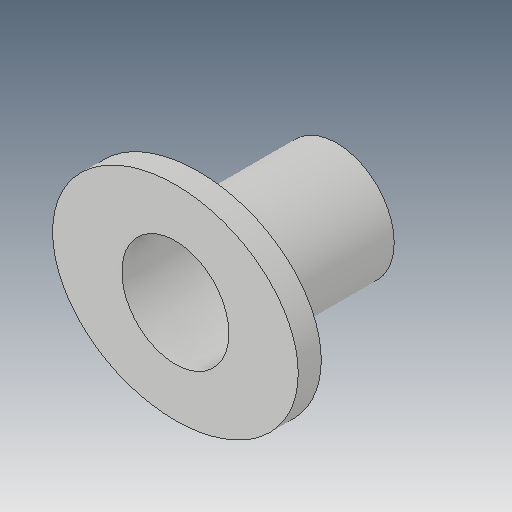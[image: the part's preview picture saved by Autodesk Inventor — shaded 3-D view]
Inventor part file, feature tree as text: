
AUTODESK INVENTOR PART (.ipt)
format: ipt  version: 2017 (Build 210142000, 142)  size: 117,760 bytes
history: native  units: mm
features: extrude x4, sketch x4, other x2, reference x1, projected_geometry x1
ambient origin geometry x8: Origin, YZ Plane, XZ Plane, XY Plane, X Axis, Y Axis, Z Axis, Center Point
bodies: Solid1 (feature_tree)
feature tree (12):
  extrude  "Extrusion1"  Depth=1.0mm TaperAngle=0.0deg
  extrude  "Extrusion2"  Depth=1.0mm TaperAngle=0.0deg
  extrude  "Extrusion3"  [1 undecoded]
  extrude  "Extrusion4"  [1 undecoded]
  sketch  "Sketch1"  dims[d0=5.0mm d1=0.0mm d2=1.0mm d3=0.0mm]
  reference  "Reference1"
  sketch  "Sketch2"  dims[d4=1.0mm d5=0.0mm d6=1.0mm d7=0.0mm]
  projected_geometry  "Projected Loop1"
  sketch  "Sketch3"
  sketch  "Sketch4"
  other  "Assembly1"
  other  "Pushfit-Adapter:1"
note: 2 required parameter values undecoded (feature->parameter linkage not recoverable at this tier; creation-order binding heuristic only, values carry confidence <= 0.55)
